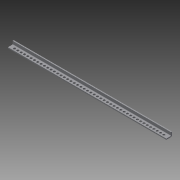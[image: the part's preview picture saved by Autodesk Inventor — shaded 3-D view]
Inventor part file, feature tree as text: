
AUTODESK INVENTOR PART (.ipt)
format: ipt  version: 2013 (Build 170138000, 138)  size: 245,248 bytes
history: native  units: in
note: dims shown in document units (in); Inventor stores cm internally (conversion verified against a paired STEP export)
features: sheet_metal_op x4, other x4, sketch x2
ambient origin geometry x8: Origin, YZ Plane, XZ Plane, XY Plane, X Axis, Y Axis, Z Axis, Center Point
bodies: Solid1 (feature_tree)
feature tree (10):
  sheet_metal_op  "Face1"
  sheet_metal_op  "Flange1"
  sketch  "Sketch1"  dims[d0=0.125in]
  other  "Plate1"
  sketch  "Sketch2"  dims[d1=0.125in d2=0.0625in d3=0.25in d4=0.125in d5=0.5in d6=90.0deg d7=0.05in d8=0.5in d9=0.125in d10=0.125in]
  other  "Plate2"
  sheet_metal_op  "Bend1"
  sheet_metal_op  "Corner1"
  other  "Definition1"
  other  "Cut1"
